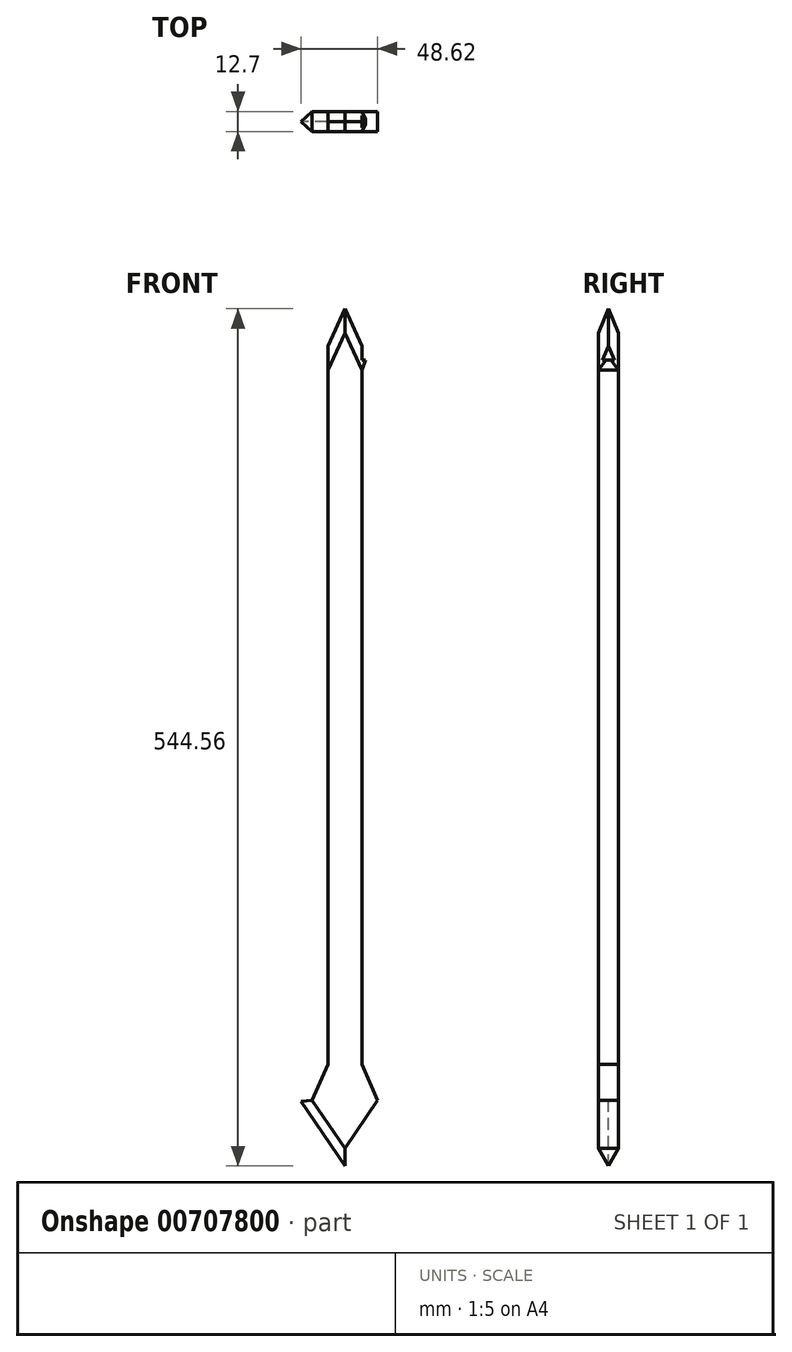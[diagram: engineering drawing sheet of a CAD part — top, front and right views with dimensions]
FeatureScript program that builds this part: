
annotation { "Feature Type Name" : "Feature", "Feature Type Description" : "" }
export const myFeature = defineFeature(function(context is Context, id is Id, definition is map)
    precondition{}
    {
        {
            var Q0;
            Q0=qCreatedBy(makeId("Front.planeOp"),FACE);
            var sketch = newSketch(context, id + "F0", { "sketchPlane" : qUnion([Q0])});
            skLineSegment(sketch, "E0", {"start": v(-27.98, 3.42) * mm, "end": v(0, -37.77) * mm});
            skLineSegment(sketch, "E1", {"start": v(0, -37.77) * mm, "end": v(27.96, 3.42) * mm});
            skLineSegment(sketch, "E2", {"start": v(-27.98, 3.42) * mm, "end": v(-17.14, 28.2) * mm});
            skLineSegment(sketch, "E3", {"start": v(27.96, 3.42) * mm, "end": v(17.08, 28.2) * mm});
            skLineSegment(sketch, "E4", {"start": v(17.08, 28.2) * mm, "end": v(27.96, 3.42) * mm});
            skLineSegment(sketch, "E5", {"start": v(-17.14, 28.2) * mm, "end": v(-17.14, 469.12) * mm});
            skLineSegment(sketch, "E6", {"start": v(-17.14, 469.12) * mm, "end": v(-17.14, 28.2) * mm});
            skLineSegment(sketch, "E7", {"start": v(17.08, 28.2) * mm, "end": v(17.08, 469.12) * mm});
            skLineSegment(sketch, "E8", {"start": v(-17.14, 469.12) * mm, "end": v(0, 506.79) * mm});
            skLineSegment(sketch, "E9", {"start": v(0, 506.79) * mm, "end": v(17.08, 469.12) * mm});
            skSolve(sketch);
        }
        {
            var Q0;
            Q0=makeQuery(id+"F0.imprint","IMPRINT",FACE,{"disambiguationData":[TD([[makeQuery(id+"F0.imprint","IMPRINT",EDGE,{"derivedFrom":sQuery(id+"F0.wireOp",EDGE,"E0")}),1.0]])]});
            extrude(context, id + "F1", {"entities" : qUnion([Q0]), "depth" : 6.35 * mm, "offsetDistance" : 25.4 * mm});
        }
        {
            var Q0;
            Q0=makeQuery(id+"F1.opExtrude","CAP_FACE",FACE,{"disambiguationData":[OSD([sQuery(id+"F0.wireOp",EDGE,"E0"),sQuery(id+"F0.wireOp",EDGE,"E1"),sQuery(id+"F0.wireOp",EDGE,"E2"),sQuery(id+"F0.wireOp",EDGE,"E4"),sQuery(id+"F0.wireOp",EDGE,"E6"),sQuery(id+"F0.wireOp",EDGE,"E7"),sQuery(id+"F0.wireOp",EDGE,"E8"),sQuery(id+"F0.wireOp",EDGE,"E9")])],"isStart":true});
            extrude(context, id + "F2", {"entities" : qUnion([Q0]), "operationType" : NewBodyOperationType.ADD, "depth" : 6.35 * mm, "offsetDistance" : 25.4 * mm});
        }
        {
            var Q0;
            Q0=makeQuery(id+"F1.opExtrude","CAP_FACE",FACE,{"disambiguationData":[OSD([sQuery(id+"F0.wireOp",EDGE,"E0"),sQuery(id+"F0.wireOp",EDGE,"E1"),sQuery(id+"F0.wireOp",EDGE,"E2"),sQuery(id+"F0.wireOp",EDGE,"E4"),sQuery(id+"F0.wireOp",EDGE,"E6"),sQuery(id+"F0.wireOp",EDGE,"E7"),sQuery(id+"F0.wireOp",EDGE,"E8"),sQuery(id+"F0.wireOp",EDGE,"E9")])],"isStart":false});
            var Q1;
            Q1=makeQuery(id+"F2.opExtrude","CAP_FACE",FACE,{"disambiguationData":[OSD([sQuery(id+"F0.wireOp",EDGE,"E0"),sQuery(id+"F0.wireOp",EDGE,"E1"),sQuery(id+"F0.wireOp",EDGE,"E2"),sQuery(id+"F0.wireOp",EDGE,"E4"),sQuery(id+"F0.wireOp",EDGE,"E6"),sQuery(id+"F0.wireOp",EDGE,"E7"),sQuery(id+"F0.wireOp",EDGE,"E8"),sQuery(id+"F0.wireOp",EDGE,"E9")])],"isStart":false});
            chamfer(context, id + "F3", {"entities" : qUnion([Q0, Q1]), "chamferType" : ChamferType.OFFSET_ANGLE, "width" : 6.35 * mm, "oppositeDirection" : false, "angle" : 45 * degree, "tangentPropagation" : true});
        }
        {
            var Q0;
            Q0=makeQuery(id+"F1.opExtrude","CAP_FACE",FACE,{"disambiguationData":[OSD([sQuery(id+"F0.wireOp",EDGE,"E0"),sQuery(id+"F0.wireOp",EDGE,"E1"),sQuery(id+"F0.wireOp",EDGE,"E2"),sQuery(id+"F0.wireOp",EDGE,"E4"),sQuery(id+"F0.wireOp",EDGE,"E6"),sQuery(id+"F0.wireOp",EDGE,"E7"),sQuery(id+"F0.wireOp",EDGE,"E8"),sQuery(id+"F0.wireOp",EDGE,"E9")])],"isStart":false});
            extrude(context, id + "F4", {"entities" : qUnion([Q0]), "operationType" : NewBodyOperationType.ADD, "depth" : 0.03 * mm, "offsetDistance" : 25.4 * mm});
        }
        {
            var Q0;
            Q0=makeQuery(id+"F2.opExtrude","CAP_FACE",FACE,{"disambiguationData":[OSD([sQuery(id+"F0.wireOp",EDGE,"E0"),sQuery(id+"F0.wireOp",EDGE,"E1"),sQuery(id+"F0.wireOp",EDGE,"E2"),sQuery(id+"F0.wireOp",EDGE,"E4"),sQuery(id+"F0.wireOp",EDGE,"E6"),sQuery(id+"F0.wireOp",EDGE,"E7"),sQuery(id+"F0.wireOp",EDGE,"E8"),sQuery(id+"F0.wireOp",EDGE,"E9")])],"isStart":false});
            extrude(context, id + "F5", {"entities" : qUnion([Q0]), "operationType" : NewBodyOperationType.ADD, "depth" : 0.03 * mm, "offsetDistance" : 25.4 * mm});
        }
        {
            var Q0;
            Q0=makeQuery(id+"F4.opExtrude","CAP_FACE",FACE,{"disambiguationData":[OSD([sQuery(id+"F0.wireOp",EDGE,"E0"),sQuery(id+"F0.wireOp",EDGE,"E1"),sQuery(id+"F0.wireOp",EDGE,"E2"),sQuery(id+"F0.wireOp",EDGE,"E4"),sQuery(id+"F0.wireOp",EDGE,"E6"),sQuery(id+"F0.wireOp",EDGE,"E7"),sQuery(id+"F0.wireOp",EDGE,"E8"),sQuery(id+"F0.wireOp",EDGE,"E9")])],"isStart":false});
            var sketch = newSketch(context, id + "F6", { "sketchPlane" : qUnion([Q0])});
            skLineSegment(sketch, "E10.bottom", {"start": v(10.73, 99.07) * mm, "end": v(32.7, 99.07) * mm});
            skLineSegment(sketch, "E10.top", {"start": v(10.73, 29.55) * mm, "end": v(32.7, 29.55) * mm});
            skLineSegment(sketch, "E10.left", {"start": v(10.73, 99.07) * mm, "end": v(10.73, 29.55) * mm});
            skLineSegment(sketch, "E10.right", {"start": v(32.7, 99.07) * mm, "end": v(32.7, 29.55) * mm});
            skLineSegment(sketch, "E11", {"start": v(10.73, 29.55) * mm, "end": v(10.73, 26.86) * mm});
            skLineSegment(sketch, "E12", {"start": v(10.73, 26.86) * mm, "end": v(24.63, -4.77) * mm});
            skLineSegment(sketch, "E13", {"start": v(24.63, -4.77) * mm, "end": v(32.22, 4.08) * mm});
            skLineSegment(sketch, "E14", {"start": v(32.22, 4.08) * mm, "end": v(20.74, 31.63) * mm});
            skLineSegment(sketch, "E15", {"start": v(20.74, 31.63) * mm, "end": v(10.73, 29.55) * mm});
            skLineSegment(sketch, "E16", {"start": v(20.74, 4.08) * mm, "end": v(29.74, -3.64) * mm});
            skLineSegment(sketch, "E17", {"start": v(29.74, -3.64) * mm, "end": v(0, -41.62) * mm});
            skLineSegment(sketch, "E18", {"start": v(0, -41.62) * mm, "end": v(0, -26.47) * mm});
            skLineSegment(sketch, "E19", {"start": v(0, -26.47) * mm, "end": v(0, -41.62) * mm});
            skLineSegment(sketch, "E20", {"start": v(0, -41.62) * mm, "end": v(-30.32, 3) * mm});
            skLineSegment(sketch, "E21", {"start": v(-30.32, 3) * mm, "end": v(-20.76, 4.09) * mm});
            skLineSegment(sketch, "E22", {"start": v(-20.76, 4.09) * mm, "end": v(0, -26.47) * mm});
            skLineSegment(sketch, "E23", {"start": v(-30.32, 3) * mm, "end": v(-18.35, 33.11) * mm});
            skLineSegment(sketch, "E24", {"start": v(-18.35, 33.11) * mm, "end": v(-10.79, 26.87) * mm});
            skLineSegment(sketch, "E25", {"start": v(-10.79, 26.87) * mm, "end": v(-20.76, 4.09) * mm});
            skLineSegment(sketch, "E26.bottom", {"start": v(-10.79, 26.87) * mm, "end": v(-21.72, 26.87) * mm});
            skLineSegment(sketch, "E26.top", {"start": v(-10.79, 486.68) * mm, "end": v(-21.72, 486.68) * mm});
            skLineSegment(sketch, "E26.left", {"start": v(-10.79, 26.87) * mm, "end": v(-10.79, 486.68) * mm});
            skLineSegment(sketch, "E26.right", {"start": v(-21.72, 26.87) * mm, "end": v(-21.72, 486.68) * mm});
            skLineSegment(sketch, "E27.bottom", {"start": v(32.7, 29.55) * mm, "end": v(10.73, 29.55) * mm});
            skLineSegment(sketch, "E27.top", {"start": v(32.7, 505.5) * mm, "end": v(10.73, 505.5) * mm});
            skLineSegment(sketch, "E27.left", {"start": v(32.7, 29.55) * mm, "end": v(32.7, 505.5) * mm});
            skLineSegment(sketch, "E27.right", {"start": v(10.73, 29.55) * mm, "end": v(10.73, 505.5) * mm});
            skLineSegment(sketch, "E28.bottom", {"start": v(10.73, 467.75) * mm, "end": v(20.74, 467.75) * mm});
            skLineSegment(sketch, "E28.top", {"start": v(10.73, 474.1) * mm, "end": v(20.74, 474.1) * mm});
            skLineSegment(sketch, "E28.left", {"start": v(10.73, 467.75) * mm, "end": v(10.73, 474.1) * mm});
            skLineSegment(sketch, "E28.right", {"start": v(20.74, 467.75) * mm, "end": v(20.74, 474.1) * mm});
            skLineSegment(sketch, "E29", {"start": v(10.73, 467.75) * mm, "end": v(19.45, 491.03) * mm});
            skLineSegment(sketch, "E30", {"start": v(19.45, 491.03) * mm, "end": v(0, 514.64) * mm});
            skLineSegment(sketch, "E31", {"start": v(0, 514.64) * mm, "end": v(-16.26, 476.1) * mm});
            skPoint(sketch, "E31.endSnap0", {"position": v(-16.26, 486.68) * mm});
            skLineSegment(sketch, "E32", {"start": v(-16.26, 476.1) * mm, "end": v(-10.79, 467.75) * mm});
            skSolve(sketch);
        }
        {
            var Q0;
            {var subQ0=sQuery(id+"F6.wireOp",EDGE,"E28.left");Q0=makeQuery(id+"F6.imprint","IMPRINT",FACE,{"disambiguationData":[TD([[makeQuery(id+"F6.imprint","IMPRINT",EDGE,{"derivedFrom":subQ0}),1.0]])]});}
            var Q1;
            {var subQ5=sQuery(id+"F6.wireOp",EDGE,"E32");Q1=makeQuery(id+"F6.imprint","IMPRINT",FACE,{"disambiguationData":[TD([[makeQuery(id+"F6.imprint","IMPRINT",EDGE,{"derivedFrom":subQ5}),1.0]])]});}
            var Q2;
            {var subQ7=sQuery(id+"F6.wireOp",EDGE,"E24");Q2=makeQuery(id+"F6.imprint","IMPRINT",FACE,{"disambiguationData":[TD([[makeQuery(id+"F6.imprint","IMPRINT",EDGE,{"derivedFrom":subQ7}),1.0]])]});}
            var Q3;
            {var subQ3=sQuery(id+"F6.wireOp",EDGE,"E30");var subQ5=sQuery(id+"F6.wireOp",EDGE,"E29");var subQ7=makeQuery(id+"F6.imprint","INTERSECT",VERTEX,{"derivedFrom":[subQ5,subQ3]});Q3=makeQuery(id+"F6.imprint","IMPRINT",FACE,{"disambiguationData":[TD([[makeQuery(id+"F6.imprint","IMPRINT",EDGE,{"disambiguationData":[TD([[subQ7,1.0]])],"derivedFrom":subQ5}),1.0]])]});}
            var Q4;
            {var subQ11=sQuery(id+"F6.wireOp",EDGE,"E10.bottom");Q4=makeQuery(id+"F6.imprint","IMPRINT",FACE,{"disambiguationData":[TD([[makeQuery(id+"F6.imprint","IMPRINT",EDGE,{"derivedFrom":subQ11}),1.0]])]});}
            var Q5;
            {var subQ0=sQuery(id+"F6.wireOp",EDGE,"E28.bottom");Q5=makeQuery(id+"F6.imprint","IMPRINT",FACE,{"disambiguationData":[TD([[makeQuery(id+"F6.imprint","IMPRINT",EDGE,{"derivedFrom":subQ0}),1.0]])]});}
            var Q6;
            {var subQ0=sQuery(id+"F6.wireOp",EDGE,"E28.left");Q6=makeQuery(id+"F6.imprint","IMPRINT",FACE,{"disambiguationData":[TD([[makeQuery(id+"F6.imprint","IMPRINT",EDGE,{"derivedFrom":subQ0}),-1.0]])]});}
            var Q7;
            {var subQ2=sQuery(id+"F6.wireOp",EDGE,"E10.bottom");Q7=makeQuery(id+"F6.imprint","IMPRINT",FACE,{"disambiguationData":[TD([[makeQuery(id+"F6.imprint","IMPRINT",EDGE,{"derivedFrom":subQ2}),-1.0]])]});}
            var Q8;
            {var subQ0=sQuery(id+"F6.wireOp",EDGE,"E24");Q8=makeQuery(id+"F6.imprint","IMPRINT",FACE,{"disambiguationData":[TD([[makeQuery(id+"F6.imprint","IMPRINT",EDGE,{"derivedFrom":subQ0}),-1.0]])]});}
            var Q9;
            {var subQ15=sQuery(id+"F6.wireOp",EDGE,"E11");Q9=makeQuery(id+"F6.imprint","IMPRINT",FACE,{"disambiguationData":[TD([[makeQuery(id+"F6.imprint","IMPRINT",EDGE,{"derivedFrom":subQ15}),-1.0]])]});}
            var Q10;
            {var subQ0=sQuery(id+"F6.wireOp",EDGE,"E21");Q10=makeQuery(id+"F6.imprint","IMPRINT",FACE,{"disambiguationData":[TD([[makeQuery(id+"F6.imprint","IMPRINT",EDGE,{"derivedFrom":subQ0}),1.0]])]});}
            var Q11;
            {var subQ0=sQuery(id+"F6.wireOp",EDGE,"E17");Q11=makeQuery(id+"F6.imprint","IMPRINT",FACE,{"disambiguationData":[TD([[makeQuery(id+"F6.imprint","IMPRINT",EDGE,{"derivedFrom":subQ0}),-1.0]])]});}
            var Q12;
            {var subQ1=sQuery(id+"F6.wireOp",EDGE,"E12");var subQ11=sQuery(id+"F6.wireOp",EDGE,"E13");var subQ12=makeQuery(id+"F6.imprint","INTERSECT",VERTEX,{"derivedFrom":[subQ1,subQ11]});Q12=makeQuery(id+"F6.imprint","IMPRINT",FACE,{"disambiguationData":[TD([[makeQuery(id+"F6.imprint","IMPRINT",EDGE,{"disambiguationData":[TD([[subQ12,-1.0]])],"derivedFrom":subQ11}),1.0]])]});}
            var Q13;
            {var subQ0=sQuery(id+"F6.wireOp",EDGE,"E15");Q13=makeQuery(id+"F6.imprint","IMPRINT",FACE,{"disambiguationData":[TD([[makeQuery(id+"F6.imprint","IMPRINT",EDGE,{"derivedFrom":subQ0}),1.0]])]});}
            var Q14;
            Q14=makeQuery(id+"F6.imprint","IMPRINT",FACE,{"disambiguationData":[TD([[makeQuery(id+"F6.imprint","IMPRINT",EDGE,{"derivedFrom":sQuery(id+"F6.wireOp",EDGE,"E19")}),-1.0]])]});
            extrude(context, id + "F7", {"entities" : qUnion([Q0, Q1, Q2, Q3, Q4, Q5, Q6, Q7, Q8, Q9, Q10, Q11, Q12, Q13, Q14]), "operationType" : NewBodyOperationType.REMOVE, "oppositeDirection" : true, "depth" : 25.4 * mm, "offsetDistance" : 25.4 * mm});
        }
        {
            var Q0;
            Q0=makeQuery(id+"F4.opExtrude","CAP_FACE",FACE,{"disambiguationData":[OSD([sQuery(id+"F0.wireOp",EDGE,"E0"),sQuery(id+"F0.wireOp",EDGE,"E1"),sQuery(id+"F0.wireOp",EDGE,"E2"),sQuery(id+"F0.wireOp",EDGE,"E4"),sQuery(id+"F0.wireOp",EDGE,"E6"),sQuery(id+"F0.wireOp",EDGE,"E7"),sQuery(id+"F0.wireOp",EDGE,"E8"),sQuery(id+"F0.wireOp",EDGE,"E9")])],"isStart":false});
            extrude(context, id + "F8", {"entities" : qUnion([Q0]), "operationType" : NewBodyOperationType.REMOVE, "oppositeDirection" : true, "depth" : 0.03 * mm, "offsetDistance" : 25.4 * mm});
        }
        {
            var Q0;
            Q0=makeQuery(id+"F5.opExtrude","CAP_FACE",FACE,{"disambiguationData":[OSD([sQuery(id+"F0.wireOp",EDGE,"E0"),sQuery(id+"F0.wireOp",EDGE,"E1"),sQuery(id+"F0.wireOp",EDGE,"E2"),sQuery(id+"F0.wireOp",EDGE,"E4"),sQuery(id+"F0.wireOp",EDGE,"E6"),sQuery(id+"F0.wireOp",EDGE,"E7"),sQuery(id+"F0.wireOp",EDGE,"E8"),sQuery(id+"F0.wireOp",EDGE,"E9")])],"isStart":false});
            extrude(context, id + "F9", {"entities" : qUnion([Q0]), "operationType" : NewBodyOperationType.REMOVE, "oppositeDirection" : true, "depth" : 0.03 * mm, "offsetDistance" : 25.4 * mm});
        }
    });
